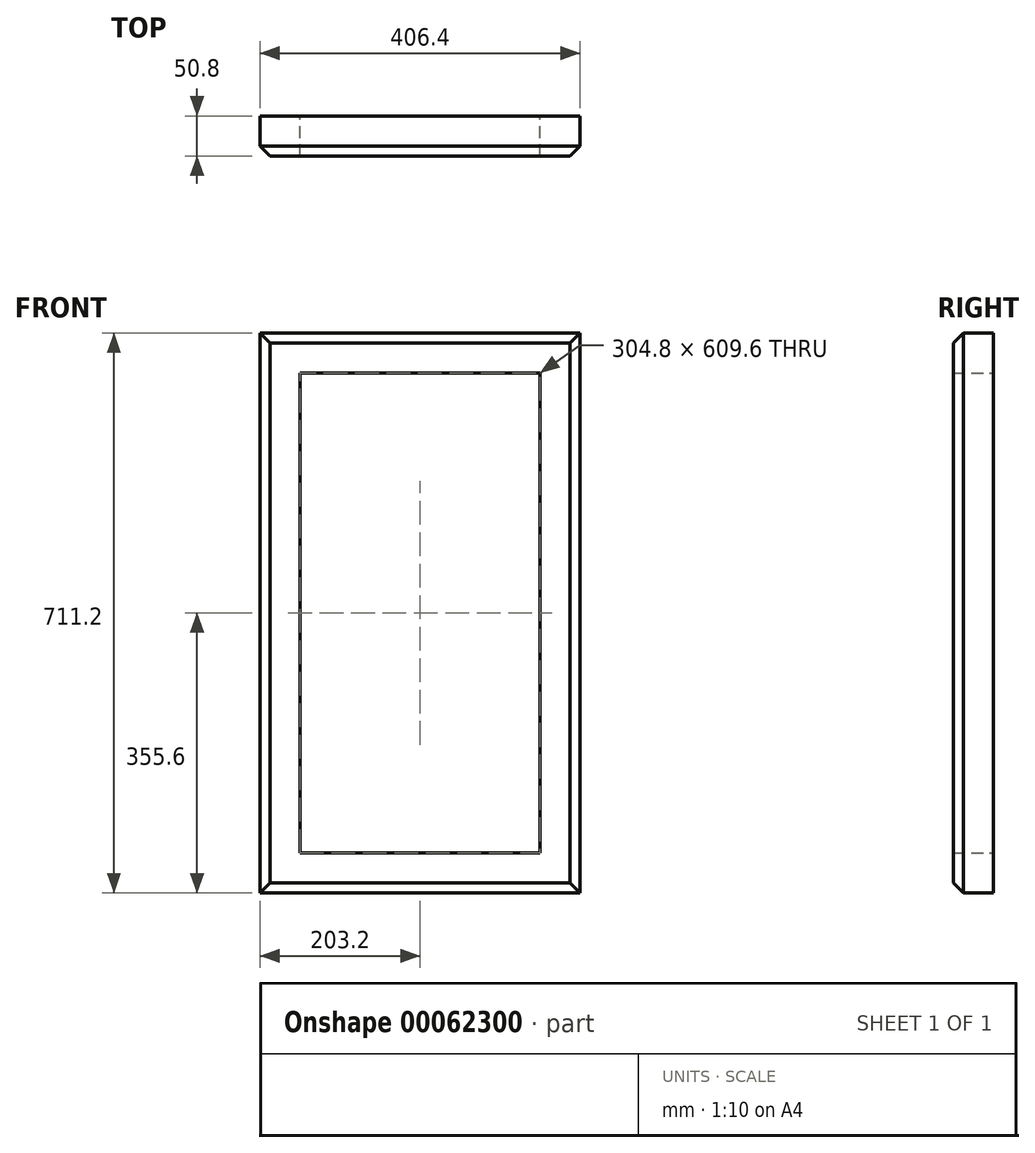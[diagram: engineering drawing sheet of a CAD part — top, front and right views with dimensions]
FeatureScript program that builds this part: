
annotation { "Feature Type Name" : "Feature", "Feature Type Description" : "" }
export const myFeature = defineFeature(function(context is Context, id is Id, definition is map)
    precondition{}
    {
        {
            var Q0;
            Q0=qCreatedBy(makeId("Front.planeOp"),FACE);
            var sketch = newSketch(context, id + "F0", { "sketchPlane" : qUnion([Q0])});
            skLineSegment(sketch, "E0.rect.bottom", {"start": v(203.2, -355.6) * mm, "end": v(-203.2, -355.6) * mm});
            skLineSegment(sketch, "E0.rect.top", {"start": v(203.2, 355.6) * mm, "end": v(-203.2, 355.6) * mm});
            skLineSegment(sketch, "E0.rect.left", {"start": v(203.2, -355.6) * mm, "end": v(203.2, 355.6) * mm});
            skLineSegment(sketch, "E0.rect.right", {"start": v(-203.2, -355.6) * mm, "end": v(-203.2, 355.6) * mm});
            skPoint(sketch, "E0.rect.middle", {"position": v(0, 0) * mm});
            skLineSegment(sketch, "E1.rect.bottom", {"start": v(152.4, -304.8) * mm, "end": v(-152.4, -304.8) * mm});
            skLineSegment(sketch, "E1.rect.top", {"start": v(152.4, 304.8) * mm, "end": v(-152.4, 304.8) * mm});
            skLineSegment(sketch, "E1.rect.left", {"start": v(152.4, -304.8) * mm, "end": v(152.4, 304.8) * mm});
            skLineSegment(sketch, "E1.rect.right", {"start": v(-152.4, -304.8) * mm, "end": v(-152.4, 304.8) * mm});
            skSolve(sketch);
        }
        {
            var Q0;
            Q0=makeQuery(id+"F0.imprint","IMPRINT",FACE,{"disambiguationData":[TD([[makeQuery(id+"F0.imprint","IMPRINT",EDGE,{"derivedFrom":sQuery(id+"F0.wireOp",EDGE,"E0.rect.bottom")}),-1.0]])]});
            extrude(context, id + "F1", {"entities" : qUnion([Q0]), "depth" : 50.8 * mm});
        }
        {
            var Q0;
            Q0=makeQuery(id+"F1.opExtrude","SWEPT_FACE",FACE,{"disambiguationData":[OSD([sQuery(id+"F0.wireOp",EDGE,"E0.rect.bottom")])]});
            var sketch = newSketch(context, id + "F2", { "sketchPlane" : qUnion([Q0])});
            skSolve(sketch);
        }
        {
            var Q0;
            Q0=makeQuery(id+"F1.opExtrude","CAP_EDGE",EDGE,{"disambiguationData":[OSD([sQuery(id+"F0.wireOp",EDGE,"E0.rect.left")])],"isStart":false});
            var Q1;
            Q1=makeQuery(id+"F1.opExtrude","CAP_EDGE",EDGE,{"disambiguationData":[OSD([sQuery(id+"F0.wireOp",EDGE,"E0.rect.top")])],"isStart":false});
            var Q2;
            Q2=makeQuery(id+"F1.opExtrude","CAP_EDGE",EDGE,{"disambiguationData":[OSD([sQuery(id+"F0.wireOp",EDGE,"E0.rect.right")])],"isStart":false});
            var Q3;
            Q3=makeQuery(id+"F1.opExtrude","CAP_EDGE",EDGE,{"disambiguationData":[OSD([sQuery(id+"F0.wireOp",EDGE,"E0.rect.bottom")])],"isStart":false});
            chamfer(context, id + "F3", {"entities" : qUnion([Q0, Q1, Q2, Q3]), "width" : 12.7 * mm, "tangentPropagation" : true});
        }
    });
